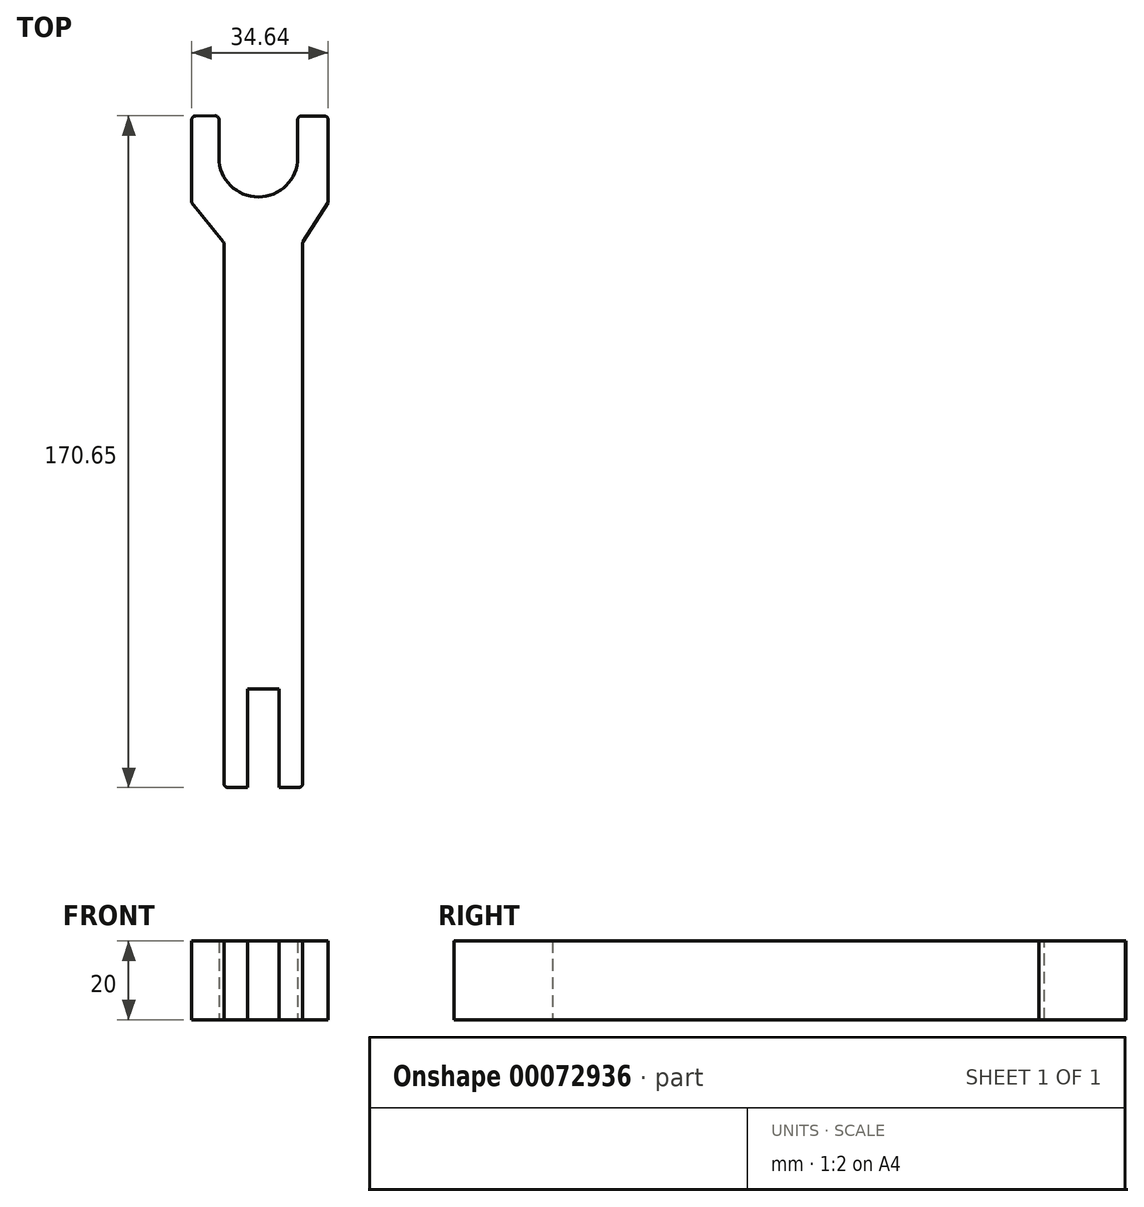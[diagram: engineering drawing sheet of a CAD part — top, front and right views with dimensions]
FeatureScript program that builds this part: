
annotation { "Feature Type Name" : "Feature", "Feature Type Description" : "" }
export const myFeature = defineFeature(function(context is Context, id is Id, definition is map)
    precondition{}
    {
        {
            var Q0;
            Q0=qCreatedBy(makeId("Top.planeOp"),FACE);
            var sketch = newSketch(context, id + "F0", { "sketchPlane" : qUnion([Q0])});
            skLineSegment(sketch, "E0.top", {"start": v(-26.45, -80) * mm, "end": v(-20.45, -80) * mm});
            skLineSegment(sketch, "E0.left", {"start": v(-26.45, 58.48) * mm, "end": v(-26.45, -80) * mm});
            skLineSegment(sketch, "E0.right", {"start": v(-6.45, 58.48) * mm, "end": v(-6.45, -80) * mm});
            skLineSegment(sketch, "E1", {"start": v(-20.45, -80) * mm, "end": v(-20.45, -55) * mm});
            skLineSegment(sketch, "E2", {"start": v(-20.45, -55) * mm, "end": v(-12.45, -55) * mm});
            skLineSegment(sketch, "E3", {"start": v(-12.45, -55) * mm, "end": v(-12.45, -80) * mm});
            skLineSegment(sketch, "E4.trimOffspring", {"start": v(-12.45, -80) * mm, "end": v(-6.45, -80) * mm});
            skLineSegment(sketch, "E5", {"start": v(-26.45, 58.48) * mm, "end": v(-34.64, 68.56) * mm});
            skLineSegment(sketch, "E6", {"start": v(-34.64, 68.56) * mm, "end": v(-34.64, 90.62) * mm});
            skLineSegment(sketch, "E7", {"start": v(-6.45, 58.48) * mm, "end": v(0, 68.56) * mm});
            skLineSegment(sketch, "E8", {"start": v(0, 68.56) * mm, "end": v(0, 90.62) * mm});
            skLineSegment(sketch, "E9", {"start": v(-7.71, 90.62) * mm, "end": v(-7.71, 70) * mm});
            skLineSegment(sketch, "E10", {"start": v(-7.71, 70) * mm, "end": v(-27.71, 70) * mm});
            skLineSegment(sketch, "E11", {"start": v(-27.71, 70) * mm, "end": v(-27.71, 90.65) * mm});
            skLineSegment(sketch, "E12", {"start": v(0, 90.62) * mm, "end": v(-7.71, 90.62) * mm});
            skLineSegment(sketch, "E13", {"start": v(-27.71, 90.65) * mm, "end": v(-34.64, 90.62) * mm});
            skSolve(sketch);
        }
        {
            var Q0;
            Q0=makeQuery(id+"F0.imprint","IMPRINT",FACE,{"disambiguationData":[TD([[makeQuery(id+"F0.imprint","IMPRINT",EDGE,{"derivedFrom":sQuery(id+"F0.wireOp",EDGE,"E0.top")}),1.0]])]});
            extrude(context, id + "F1", {"entities" : qUnion([Q0]), "depth" : 20 * mm});
        }
        {
            var Q0;
            Q0=makeQuery(id+"F1.opExtrude","SWEPT_EDGE",EDGE,{"disambiguationData":[OSD([sQuery(id+"F0.wireOp",EDGE,"E0.right"),sQuery(id+"F0.wireOp",EDGE,"0c261594-dc4d-429c-8ef3-e7b9badb0c77.trimOffspring")])]});
            var Q1;
            Q1=makeQuery(id+"F1.opExtrude","SWEPT_EDGE",EDGE,{"disambiguationData":[OSD([sQuery(id+"F0.wireOp",EDGE,"E0.bottom"),sQuery(id+"F0.wireOp",EDGE,"E0.left")])]});
            var Q2;
            Q2=makeQuery(id+"F1.opExtrude","SWEPT_EDGE",EDGE,{"disambiguationData":[OSD([sQuery(id+"F0.wireOp",EDGE,"E0.top"),sQuery(id+"F0.wireOp",EDGE,"E0.left")])]});
            var Q3;
            Q3=makeQuery(id+"F1.opExtrude","SWEPT_EDGE",EDGE,{"disambiguationData":[OSD([sQuery(id+"F0.wireOp",EDGE,"E0.right"),sQuery(id+"F0.wireOp",EDGE,"E4.trimOffspring")])]});
            fillet(context, id + "F2", {"entities" : qUnion([Q0, Q1, Q2, Q3]), "radius" : 1 * mm, "tangentPropagation" : true, "allowEdgeOverflow" : false});
        }
        {
            var Q0;
            Q0=makeQuery(id+"F1.opExtrude","SWEPT_EDGE",EDGE,{"disambiguationData":[OSD([sQuery(id+"F0.wireOp",EDGE,"E9"),sQuery(id+"F0.wireOp",EDGE,"E10")])]});
            var Q1;
            Q1=makeQuery(id+"F1.opExtrude","SWEPT_EDGE",EDGE,{"disambiguationData":[OSD([sQuery(id+"F0.wireOp",EDGE,"E10"),sQuery(id+"F0.wireOp",EDGE,"E11")])]});
            fillet(context, id + "F3", {"entities" : qUnion([Q0, Q1]), "radius" : 10 * mm, "tangentPropagation" : true, "allowEdgeOverflow" : false});
        }
        {
            var Q0;
            Q0=makeQuery(id+"F1.opExtrude","SWEPT_EDGE",EDGE,{"disambiguationData":[OSD([sQuery(id+"F0.wireOp",EDGE,"E11"),sQuery(id+"F0.wireOp",EDGE,"E13")])]});
            var Q1;
            Q1=makeQuery(id+"F1.opExtrude","SWEPT_EDGE",EDGE,{"disambiguationData":[OSD([sQuery(id+"F0.wireOp",EDGE,"E6"),sQuery(id+"F0.wireOp",EDGE,"E13")])]});
            var Q2;
            Q2=makeQuery(id+"F1.opExtrude","SWEPT_EDGE",EDGE,{"disambiguationData":[OSD([sQuery(id+"F0.wireOp",EDGE,"E9"),sQuery(id+"F0.wireOp",EDGE,"E12")])]});
            var Q3;
            Q3=makeQuery(id+"F1.opExtrude","SWEPT_EDGE",EDGE,{"disambiguationData":[OSD([sQuery(id+"F0.wireOp",EDGE,"E8"),sQuery(id+"F0.wireOp",EDGE,"E12")])]});
            fillet(context, id + "F4", {"entities" : qUnion([Q0, Q1, Q2, Q3]), "radius" : 1 * mm, "tangentPropagation" : true, "allowEdgeOverflow" : false});
        }
    });
